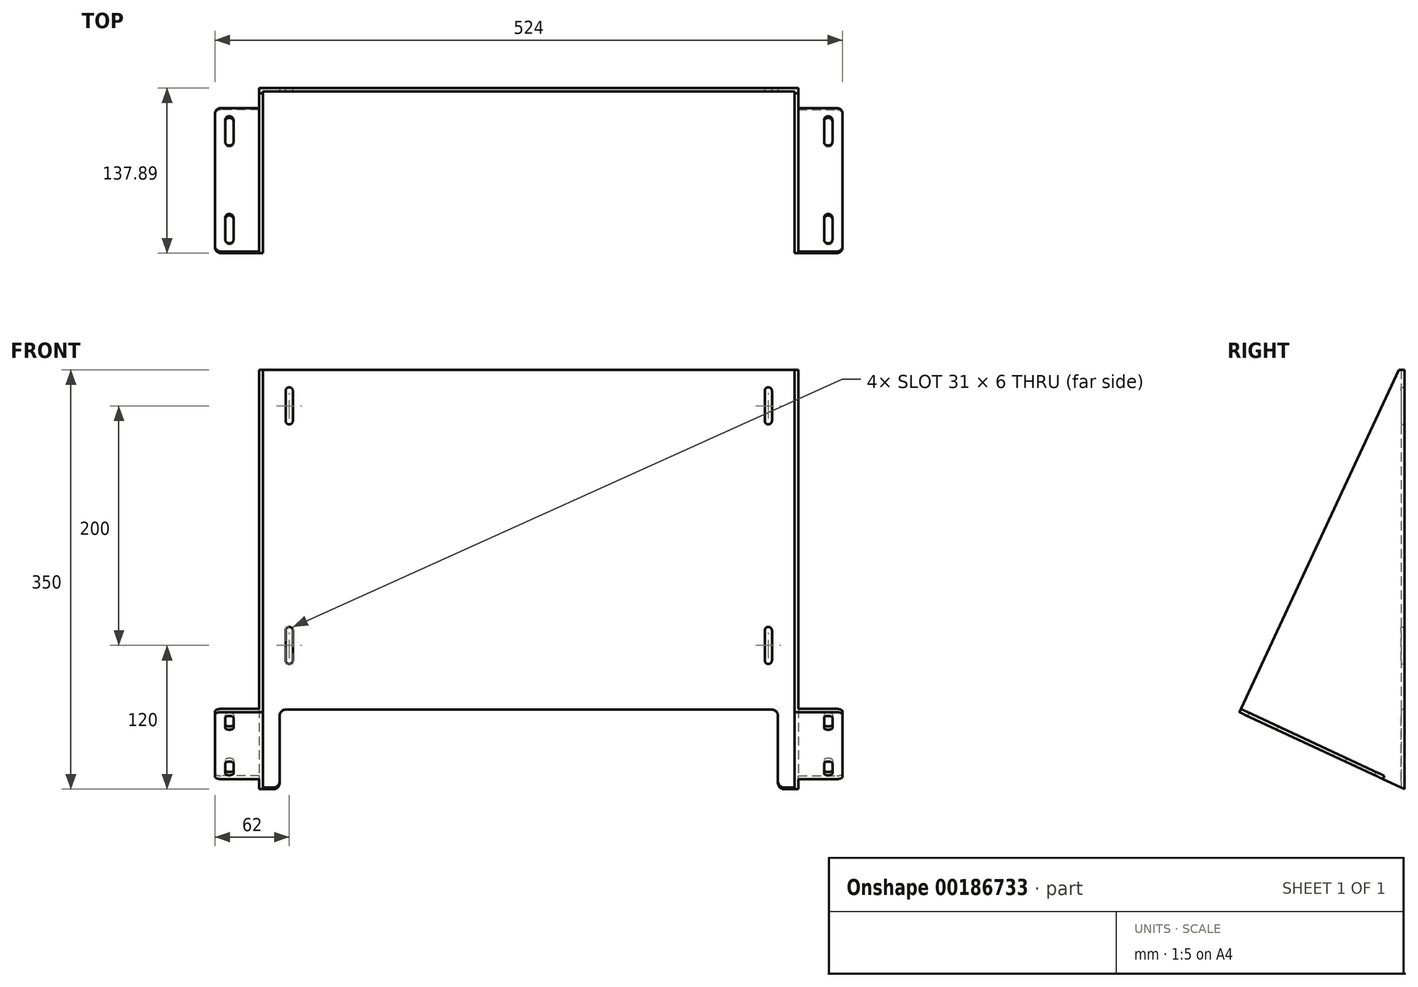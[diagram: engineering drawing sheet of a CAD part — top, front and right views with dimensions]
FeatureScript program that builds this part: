
annotation { "Feature Type Name" : "Feature", "Feature Type Description" : "" }
export const myFeature = defineFeature(function(context is Context, id is Id, definition is map)
    precondition{}
    {
        {
            var Q0;
            Q0=qCreatedBy(makeId("Right.planeOp"),FACE);
            var sketch = newSketch(context, id + "F0", { "sketchPlane" : qUnion([Q0])});
            skLineSegment(sketch, "E0", {"start": v(0, 360) * mm, "end": v(-167.87, 0) * mm});
            skLineSegment(sketch, "E1", {"start": v(-167.87, 0) * mm, "end": v(0, 0) * mm});
            skLineSegment(sketch, "E2", {"start": v(0, 0) * mm, "end": v(0, 360) * mm});
            skSolve(sketch);
        }
        {
            var Q0;
            Q0 = qSketchRegion(id + "F0", true);
            extrude(context, id + "F1", {"entities" : qUnion([Q0]), "depth" : 450 * mm});
        }
        {
            var Q0;
            Q0=makeQuery(id+"F1.opExtrude","SWEPT_FACE",FACE,{"disambiguationData":[OSD([sQuery(id+"F0.wireOp",EDGE,"E1")])]});
            var sketch = newSketch(context, id + "F2", { "sketchPlane" : qUnion([Q0])});
            skLineSegment(sketch, "E3", {"start": v(225, 0) * mm, "end": v(225, 167.87) * mm, "construction": true});
            skLineSegment(sketch, "E4.bottom", {"start": v(447, 167.87) * mm, "end": v(3, 167.87) * mm});
            skLineSegment(sketch, "E4.top", {"start": v(447, 3) * mm, "end": v(3, 3) * mm});
            skLineSegment(sketch, "E4.left", {"start": v(447, 167.87) * mm, "end": v(447, 3) * mm});
            skLineSegment(sketch, "E4.right", {"start": v(3, 167.87) * mm, "end": v(3, 3) * mm});
            skPoint(sketch, "E4.middle", {"position": v(225, 85.44) * mm});
            skSolve(sketch);
        }
        {
            var Q0;
            Q0 = qSketchRegion(id + "F2", true);
            extrude(context, id + "F3", {"entities" : qUnion([Q0]), "operationType" : NewBodyOperationType.REMOVE, "endBound" : BoundingType.THROUGH_ALL, "oppositeDirection" : true, "depth" : 25 * mm});
        }
        {
            var Q0;
            Q0=makeQuery(id+"F1.opExtrude","CAP_FACE",FACE,{"disambiguationData":[OSD([sQuery(id+"F0.wireOp",EDGE,"E0"),sQuery(id+"F0.wireOp",EDGE,"E1"),sQuery(id+"F0.wireOp",EDGE,"E2")])],"isStart":true});
            var sketch = newSketch(context, id + "F4", { "sketchPlane" : qUnion([Q0])});
            skLineSegment(sketch, "E5", {"start": v(137.89, 64.3) * mm, "end": v(167.87, 0) * mm});
            skLineSegment(sketch, "E6", {"start": v(167.87, 0) * mm, "end": v(0, 0) * mm});
            skLineSegment(sketch, "E7", {"start": v(0, 0) * mm, "end": v(137.89, 64.3) * mm});
            skSolve(sketch);
        }
        {
            var Q0;
            Q0 = qSketchRegion(id + "F4", true);
            extrude(context, id + "F5", {"entities" : qUnion([Q0]), "operationType" : NewBodyOperationType.REMOVE, "endBound" : BoundingType.THROUGH_ALL, "oppositeDirection" : true, "depth" : 25 * mm});
        }
        {
            var Q0;
            Q0=makeQuery(id+"F5.boolean.opBoolean","COPY",FACE,{"derivedFrom":makeQuery(id+"F5.opExtrude","SWEPT_FACE",FACE,{"disambiguationData":[OSD([sQuery(id+"F4.wireOp",EDGE,"E7")])]})});
            var sketch = newSketch(context, id + "F6", { "sketchPlane" : qUnion([Q0])});
            skLineSegment(sketch, "E8", {"start": v(225, 3.31) * mm, "end": v(225, 86.64) * mm, "construction": true});
            skLineSegment(sketch, "E9.bottom", {"start": v(3, 152.14) * mm, "end": v(-37, 152.14) * mm});
            skLineSegment(sketch, "E9.top", {"start": v(3, 20) * mm, "end": v(-37, 20) * mm});
            skLineSegment(sketch, "E9.left", {"start": v(3, 152.14) * mm, "end": v(3, 20) * mm});
            skLineSegment(sketch, "E9.right", {"start": v(-37, 152.14) * mm, "end": v(-37, 20) * mm});
            skLineSegment(sketch, "E10.MirrorCS", {"start": v(447, 20) * mm, "end": v(487, 20) * mm});
            skLineSegment(sketch, "E11.MirrorCS", {"start": v(487, 152.14) * mm, "end": v(487, 20) * mm});
            skLineSegment(sketch, "E12.MirrorCS", {"start": v(447, 152.14) * mm, "end": v(487, 152.14) * mm});
            skLineSegment(sketch, "E13.MirrorCS", {"start": v(447, 152.14) * mm, "end": v(447, 20) * mm});
            skSolve(sketch);
        }
        {
            var Q0;
            Q0 = qSketchRegion(id + "F6", true);
            extrude(context, id + "F7", {"entities" : qUnion([Q0]), "operationType" : NewBodyOperationType.ADD, "oppositeDirection" : true, "depth" : 3 * mm});
        }
        {
            var Q0;
            Q0=makeQuery(id+"F7.opExtrude","SWEPT_EDGE",EDGE,{"disambiguationData":[OSD([sQuery(id+"F6.wireOp",EDGE,"E9.bottom"),sQuery(id+"F6.wireOp",EDGE,"E9.right")])]});
            fillet(context, id + "F8", {"entities" : qUnion([Q0]), "radius" : 5 * mm, "tangentPropagation" : true, "allowEdgeOverflow" : false});
        }
        {
            var Q0;
            Q0=makeQuery(id+"F7.opExtrude","SWEPT_EDGE",EDGE,{"disambiguationData":[OSD([sQuery(id+"F6.wireOp",EDGE,"E11.MirrorCS"),sQuery(id+"F6.wireOp",EDGE,"E12.MirrorCS")])]});
            fillet(context, id + "F9", {"entities" : qUnion([Q0]), "radius" : 5 * mm, "tangentPropagation" : true, "allowEdgeOverflow" : false});
        }
        {
            var Q0;
            Q0=makeQuery(id+"F7.opExtrude","SWEPT_EDGE",EDGE,{"disambiguationData":[OSD([sQuery(id+"F6.wireOp",EDGE,"E10.MirrorCS"),sQuery(id+"F6.wireOp",EDGE,"E11.MirrorCS")])]});
            fillet(context, id + "F10", {"entities" : qUnion([Q0]), "radius" : 5 * mm, "tangentPropagation" : true, "allowEdgeOverflow" : false});
        }
        {
            var Q0;
            Q0=makeQuery(id+"F7.opExtrude","SWEPT_EDGE",EDGE,{"disambiguationData":[OSD([sQuery(id+"F6.wireOp",EDGE,"E9.top"),sQuery(id+"F6.wireOp",EDGE,"E9.right")])]});
            fillet(context, id + "F11", {"entities" : qUnion([Q0]), "radius" : 5 * mm, "tangentPropagation" : true, "allowEdgeOverflow" : false});
        }
        {
            var Q0;
            Q0=makeQuery(id+"F7.boolean.opBoolean","MERGE",FACE,{"derivedFrom":[makeQuery(id+"F5.boolean.opBoolean","COPY",FACE,{"derivedFrom":makeQuery(id+"F5.opExtrude","SWEPT_FACE",FACE,{"disambiguationData":[OSD([sQuery(id+"F4.wireOp",EDGE,"E7")])]})}),makeQuery(id+"F7.opExtrude","CAP_FACE",FACE,{"disambiguationData":[OSD([sQuery(id+"F6.wireOp",EDGE,"E9.bottom"),sQuery(id+"F6.wireOp",EDGE,"E9.top"),sQuery(id+"F6.wireOp",EDGE,"E9.left"),sQuery(id+"F6.wireOp",EDGE,"E9.right")])],"isStart":true}),makeQuery(id+"F7.opExtrude","CAP_FACE",FACE,{"disambiguationData":[OSD([sQuery(id+"F6.wireOp",EDGE,"E10.MirrorCS"),sQuery(id+"F6.wireOp",EDGE,"E11.MirrorCS"),sQuery(id+"F6.wireOp",EDGE,"E12.MirrorCS"),sQuery(id+"F6.wireOp",EDGE,"E13.MirrorCS")])],"isStart":true})]});
            var sketch = newSketch(context, id + "F12", { "sketchPlane" : qUnion([Q0])});
            skLineSegment(sketch, "E14", {"start": v(-25, 152.14) * mm, "end": v(-25, 20) * mm, "construction": true});
            skCircle(sketch, "E15", {"center": v(-25, 131.07) * mm, "radius": 3 * mm, "construction": true});
            skLineSegment(sketch, "E16", {"start": v(225, 3.31) * mm, "end": v(225, 96.32) * mm, "construction": true});
            skCircle(sketch, "E17.MirrorC", {"center": v(475, 131.07) * mm, "radius": 3 * mm, "construction": true});
            skPoint(sketch, "E18.endSnap0", {"position": v(-25, 86.07) * mm});
            skLineSegment(sketch, "E19", {"start": v(-37, 86.07) * mm, "end": v(-89.56, 86.07) * mm, "construction": true});
            skCircle(sketch, "E20.MirrorC", {"center": v(-25, 41.07) * mm, "radius": 3 * mm, "construction": true});
            skCircle(sketch, "E21.MirrorC", {"center": v(475, 41.07) * mm, "radius": 3 * mm, "construction": true});
            skLineSegment(sketch, "E22.left", {"start": v(-21.5, 121.07) * mm, "end": v(-21.5, 141.07) * mm});
            skLineSegment(sketch, "E22.right", {"start": v(-28.5, 121.07) * mm, "end": v(-28.5, 141.07) * mm});
            skArc(sketch, "E23", {"start": v(-21.5, 141.07) * mm, "mid": v(-25, 144.57) * mm, "end": v(-28.5, 141.07) * mm});
            skLineSegment(sketch, "E24.MirrorCS", {"start": v(-28.5, 51.07) * mm, "end": v(-28.5, 31.07) * mm});
            skLineSegment(sketch, "E25.MirrorCS", {"start": v(-21.5, 51.07) * mm, "end": v(-21.5, 31.07) * mm});
            skLineSegment(sketch, "E26", {"start": v(-28.5, 141.07) * mm, "end": v(-21.5, 141.07) * mm, "construction": true});
            skArc(sketch, "E27", {"start": v(-28.5, 121.07) * mm, "mid": v(-25, 117.57) * mm, "end": v(-21.5, 121.07) * mm});
            skArc(sketch, "E28.MirrorCS", {"start": v(-21.5, 31.07) * mm, "mid": v(-25, 27.57) * mm, "end": v(-28.5, 31.07) * mm});
            skArc(sketch, "E29.MirrorCS", {"start": v(-28.5, 51.07) * mm, "mid": v(-25, 54.57) * mm, "end": v(-21.5, 51.07) * mm});
            skArc(sketch, "E30.MirrorCS", {"start": v(478.5, 121.07) * mm, "mid": v(475, 117.57) * mm, "end": v(471.5, 121.07) * mm});
            skArc(sketch, "E31.MirrorCS", {"start": v(471.5, 141.07) * mm, "mid": v(475, 144.57) * mm, "end": v(478.5, 141.07) * mm});
            skLineSegment(sketch, "E32.MirrorCS", {"start": v(471.5, 121.07) * mm, "end": v(471.5, 141.07) * mm});
            skLineSegment(sketch, "E33.MirrorCS", {"start": v(478.5, 121.07) * mm, "end": v(478.5, 141.07) * mm});
            skArc(sketch, "E34.MirrorCS", {"start": v(478.5, 51.07) * mm, "mid": v(475, 54.57) * mm, "end": v(471.5, 51.07) * mm});
            skLineSegment(sketch, "E35.MirrorCS", {"start": v(471.5, 51.07) * mm, "end": v(471.5, 31.07) * mm});
            skLineSegment(sketch, "E36.MirrorCS", {"start": v(478.5, 51.07) * mm, "end": v(478.5, 31.07) * mm});
            skArc(sketch, "E37.MirrorCS", {"start": v(471.5, 31.07) * mm, "mid": v(475, 27.57) * mm, "end": v(478.5, 31.07) * mm});
            skSolve(sketch);
        }
        {
            var Q0;
            Q0 = qSketchRegion(id + "F12", true);
            extrude(context, id + "F13", {"entities" : qUnion([Q0]), "operationType" : NewBodyOperationType.REMOVE, "endBound" : BoundingType.THROUGH_ALL, "oppositeDirection" : true, "depth" : 25 * mm});
        }
        {
            var Q0;
            Q0=makeQuery(id+"F1.opExtrude","SWEPT_FACE",FACE,{"disambiguationData":[OSD([sQuery(id+"F0.wireOp",EDGE,"E2")])]});
            var sketch = newSketch(context, id + "F14", { "sketchPlane" : qUnion([Q0])});
            skLineSegment(sketch, "E38", {"start": v(-225, 0) * mm, "end": v(-225, 182.9) * mm, "construction": true});
            skLineSegment(sketch, "E39.bottom", {"start": v(-422, 307.5) * mm, "end": v(-428, 307.5) * mm, "construction": true});
            skLineSegment(sketch, "E39.top", {"start": v(-422, 332.5) * mm, "end": v(-428, 332.5) * mm, "construction": true});
            skLineSegment(sketch, "E39.left", {"start": v(-422, 307.5) * mm, "end": v(-422, 332.5) * mm});
            skLineSegment(sketch, "E39.right", {"start": v(-428, 307.5) * mm, "end": v(-428, 332.5) * mm});
            skPoint(sketch, "E39.middle", {"position": v(-425, 320) * mm});
            skLineSegment(sketch, "E40", {"start": v(-425, 271.24) * mm, "end": v(-425, 332.5) * mm, "construction": true});
            skPoint(sketch, "E40.endSnap0", {"position": v(-425, 307.5) * mm});
            skArc(sketch, "E41", {"start": v(-422, 332.5) * mm, "mid": v(-425, 335.5) * mm, "end": v(-428, 332.5) * mm});
            skLineSegment(sketch, "E42", {"start": v(-428, 320) * mm, "end": v(-422, 320) * mm, "construction": true});
            skArc(sketch, "E43.MirrorCS", {"start": v(-422, 307.5) * mm, "mid": v(-425, 304.5) * mm, "end": v(-428, 307.5) * mm});
            skArc(sketch, "E44.MirrorCS", {"start": v(-28, 307.5) * mm, "mid": v(-25, 304.5) * mm, "end": v(-22, 307.5) * mm});
            skArc(sketch, "E45.MirrorCS", {"start": v(-28, 332.5) * mm, "mid": v(-25, 335.5) * mm, "end": v(-22, 332.5) * mm});
            skLineSegment(sketch, "E46.MirrorCS", {"start": v(-22, 307.5) * mm, "end": v(-22, 332.5) * mm});
            skLineSegment(sketch, "E47.MirrorCS", {"start": v(-28, 307.5) * mm, "end": v(-28, 332.5) * mm});
            skLineSegment(sketch, "E48", {"start": v(-401.03, 220) * mm, "end": v(-86.8, 220) * mm, "construction": true});
            skLineSegment(sketch, "E49.MirrorCS", {"start": v(-428, 132.5) * mm, "end": v(-428, 107.5) * mm});
            skLineSegment(sketch, "E50.MirrorCS", {"start": v(-422, 132.5) * mm, "end": v(-422, 107.5) * mm});
            skArc(sketch, "E51.MirrorCS", {"start": v(-422, 132.5) * mm, "mid": v(-425, 135.5) * mm, "end": v(-428, 132.5) * mm});
            skArc(sketch, "E52.MirrorCS", {"start": v(-422, 107.5) * mm, "mid": v(-425, 104.5) * mm, "end": v(-428, 107.5) * mm});
            skLineSegment(sketch, "E53.MirrorCS", {"start": v(-28, 132.5) * mm, "end": v(-28, 107.5) * mm});
            skArc(sketch, "E54.MirrorCS", {"start": v(-28, 107.5) * mm, "mid": v(-25, 104.5) * mm, "end": v(-22, 107.5) * mm});
            skLineSegment(sketch, "E55.MirrorCS", {"start": v(-22, 132.5) * mm, "end": v(-22, 107.5) * mm});
            skArc(sketch, "E56.MirrorCS", {"start": v(-28, 132.5) * mm, "mid": v(-25, 135.5) * mm, "end": v(-22, 132.5) * mm});
            skSolve(sketch);
        }
        {
            var Q0;
            Q0 = qSketchRegion(id + "F14", true);
            extrude(context, id + "F15", {"entities" : qUnion([Q0]), "operationType" : NewBodyOperationType.REMOVE, "oppositeDirection" : true, "depth" : 25 * mm});
        }
        {
            var Q0;
            Q0=makeQuery(id+"F3.boolean.opBoolean","COPY",FACE,{"derivedFrom":makeQuery(id+"F3.opExtrude","SWEPT_FACE",FACE,{"disambiguationData":[OSD([sQuery(id+"F2.wireOp",EDGE,"E4.top")])]})});
            var sketch = newSketch(context, id + "F16", { "sketchPlane" : qUnion([Q0])});
            skLineSegment(sketch, "E57", {"start": v(225, 0) * mm, "end": v(225, 110.92) * mm, "construction": true});
            skLineSegment(sketch, "E58.bottom", {"start": v(17, 0) * mm, "end": v(433, 0) * mm});
            skLineSegment(sketch, "E58.top", {"start": v(17, 66.4) * mm, "end": v(433, 66.4) * mm});
            skLineSegment(sketch, "E58.left", {"start": v(17, 0) * mm, "end": v(17, 66.4) * mm});
            skLineSegment(sketch, "E58.right", {"start": v(433, 0) * mm, "end": v(433, 66.4) * mm});
            skPoint(sketch, "E58.middle", {"position": v(225, 33.2) * mm});
            skSolve(sketch);
        }
        {
            var Q0;
            Q0 = qSketchRegion(id + "F16", true);
            extrude(context, id + "F17", {"entities" : qUnion([Q0]), "operationType" : NewBodyOperationType.REMOVE, "oppositeDirection" : true, "depth" : 25 * mm});
        }
        {
            var Q0;
            Q0=makeQuery(id+"F1.opExtrude","SWEPT_FACE",FACE,{"disambiguationData":[OSD([sQuery(id+"F0.wireOp",EDGE,"E2")])]});
            var sketch = newSketch(context, id + "F18", { "sketchPlane" : qUnion([Q0])});
            skLineSegment(sketch, "E59.bottom", {"start": v(-450, 360) * mm, "end": v(0, 360) * mm});
            skLineSegment(sketch, "E59.top", {"start": v(-450, 350) * mm, "end": v(0, 350) * mm});
            skLineSegment(sketch, "E59.left", {"start": v(-450, 360) * mm, "end": v(-450, 350) * mm});
            skLineSegment(sketch, "E59.right", {"start": v(0, 360) * mm, "end": v(0, 350) * mm});
            skSolve(sketch);
        }
        {
            var Q0;
            Q0 = qSketchRegion(id + "F18", true);
            extrude(context, id + "F19", {"entities" : qUnion([Q0]), "operationType" : NewBodyOperationType.REMOVE, "endBound" : BoundingType.THROUGH_ALL, "oppositeDirection" : true, "depth" : 25 * mm});
        }
        {
            var Q0;
            Q0=makeQuery(id+"F17.boolean.opBoolean","INTERSECT",EDGE,{"derivedFrom":[makeQuery(id+"F7.boolean.opBoolean","MERGE",FACE,{"derivedFrom":[makeQuery(id+"F5.boolean.opBoolean","COPY",FACE,{"derivedFrom":makeQuery(id+"F5.opExtrude","SWEPT_FACE",FACE,{"disambiguationData":[OSD([sQuery(id+"F4.wireOp",EDGE,"E7")])]})}),makeQuery(id+"F7.opExtrude","CAP_FACE",FACE,{"disambiguationData":[OSD([sQuery(id+"F6.wireOp",EDGE,"E9.bottom"),sQuery(id+"F6.wireOp",EDGE,"E9.top"),sQuery(id+"F6.wireOp",EDGE,"E9.left"),sQuery(id+"F6.wireOp",EDGE,"E9.right")])],"isStart":true}),makeQuery(id+"F7.opExtrude","CAP_FACE",FACE,{"disambiguationData":[OSD([sQuery(id+"F6.wireOp",EDGE,"E10.MirrorCS"),sQuery(id+"F6.wireOp",EDGE,"E11.MirrorCS"),sQuery(id+"F6.wireOp",EDGE,"E12.MirrorCS"),sQuery(id+"F6.wireOp",EDGE,"E13.MirrorCS")])],"isStart":true})]}),makeQuery(id+"F17.opExtrude","SWEPT_FACE",FACE,{"disambiguationData":[OSD([sQuery(id+"F16.wireOp",EDGE,"E58.left")])]})]});
            fillet(context, id + "F20", {"entities" : qUnion([Q0]), "radius" : 5 * mm, "tangentPropagation" : true, "allowEdgeOverflow" : false});
        }
        {
            var Q0;
            Q0=makeQuery(id+"F17.boolean.opBoolean","COPY",EDGE,{"derivedFrom":makeQuery(id+"F17.opExtrude","SWEPT_EDGE",EDGE,{"disambiguationData":[OSD([sQuery(id+"F16.wireOp",EDGE,"E58.top"),sQuery(id+"F16.wireOp",EDGE,"E58.left")])]})});
            fillet(context, id + "F21", {"entities" : qUnion([Q0]), "radius" : 5 * mm, "tangentPropagation" : true, "allowEdgeOverflow" : false});
        }
        {
            var Q0;
            Q0=makeQuery(id+"F17.boolean.opBoolean","COPY",EDGE,{"derivedFrom":makeQuery(id+"F17.opExtrude","SWEPT_EDGE",EDGE,{"disambiguationData":[OSD([sQuery(id+"F16.wireOp",EDGE,"E58.top"),sQuery(id+"F16.wireOp",EDGE,"E58.right")])]})});
            var Q1;
            Q1=makeQuery(id+"F17.boolean.opBoolean","INTERSECT",EDGE,{"derivedFrom":[makeQuery(id+"F7.boolean.opBoolean","MERGE",FACE,{"derivedFrom":[makeQuery(id+"F5.boolean.opBoolean","COPY",FACE,{"derivedFrom":makeQuery(id+"F5.opExtrude","SWEPT_FACE",FACE,{"disambiguationData":[OSD([sQuery(id+"F4.wireOp",EDGE,"E7")])]})}),makeQuery(id+"F7.opExtrude","CAP_FACE",FACE,{"disambiguationData":[OSD([sQuery(id+"F6.wireOp",EDGE,"E9.bottom"),sQuery(id+"F6.wireOp",EDGE,"E9.top"),sQuery(id+"F6.wireOp",EDGE,"E9.left"),sQuery(id+"F6.wireOp",EDGE,"E9.right")])],"isStart":true}),makeQuery(id+"F7.opExtrude","CAP_FACE",FACE,{"disambiguationData":[OSD([sQuery(id+"F6.wireOp",EDGE,"E10.MirrorCS"),sQuery(id+"F6.wireOp",EDGE,"E11.MirrorCS"),sQuery(id+"F6.wireOp",EDGE,"E12.MirrorCS"),sQuery(id+"F6.wireOp",EDGE,"E13.MirrorCS")])],"isStart":true})]}),makeQuery(id+"F17.opExtrude","SWEPT_FACE",FACE,{"disambiguationData":[OSD([sQuery(id+"F16.wireOp",EDGE,"E58.right")])]})]});
            fillet(context, id + "F22", {"entities" : qUnion([Q0, Q1]), "radius" : 5 * mm, "tangentPropagation" : true, "allowEdgeOverflow" : false});
        }
    });
